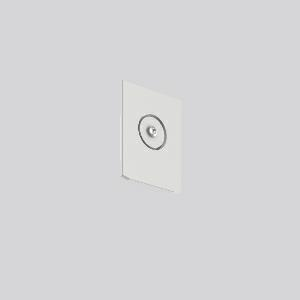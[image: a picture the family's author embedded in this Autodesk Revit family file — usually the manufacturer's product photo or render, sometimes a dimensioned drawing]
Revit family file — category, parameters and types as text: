
# Revit family: linedo_endkappe_s_f_982699_009_5f10
name_source: partatom
category: Lighting Fixtures
units: mm (PartAtom-declared; Revit-internal decimal feet)

## family parameters
Cut with Voids When Loaded = No
Host = Face
Light Source = No
Part Type = Normal
Room Calculation Point = No
Round Connector Dimension = Use Diameter
Shared = No

## types (1)
- LINEDO_Endkappe_S_F
    Apparent Load = 0 VA
    Default Elevation = 1800 mm
    Description = End cap low profile for LINEDO socket. Plastic end cap to cover the LINEDO plug system at the end of the line. Fastening by TX20 screw. Installation accessories included.
Colour: grey
Length: 16 mm
Width: 58 mm
Height: 76 mm
Weight: 21,5 g
    Height = 76 mm
    Lamp = 0 x
    Length = 17 mm
    Luminous efficacy = 0 lm/W
    Manufacturer = RZB
    ModVariant = No
    Model = 982699.009
    Mounting Place = Ceiling
    Mounting Type = Surface mounted, Pendant
    Number of Poles = 1
    OnlyDefault = Yes
    Power Factor = 1
    Product Name = LINEDO_Endkappe_S_F
    Product group = Surface mounted continuous line luminaire system
    ProductGroupID = 310
    Protection Class = Protection class
    Protection Degree = Degree of protection
    RLX_Detail_Level = 1
    RLX_Emergency_Light_Flux = 0 lm
    RLX_Emergency_Type = 0
    RLX_Emergency_Type_DB = No
    RlxData = <blob elided: 8189 chars, md5=8393a239>
    Standby Power = 0 W
    System Light Flux = 0 lm
    System Power = 0 W
    Type Comments = Product without accessories
    Type Image = 982699.009.jpg
    URL = http://relux.com
    VarID = ---
    Voltage = 0 V
    Weight = 0.00 kg
    Width = 58 mm

## geometry (parser evidence)
native form markers: Blend x2, Sweep x9
no freeform markers — native parametric forms only
